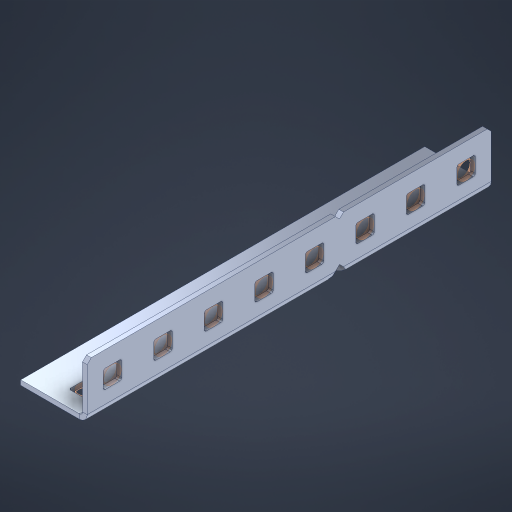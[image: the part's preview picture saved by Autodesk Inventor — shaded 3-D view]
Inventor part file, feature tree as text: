
AUTODESK INVENTOR PART (.ipt)
format: ipt  version: 2023 (Build 270158000, 158)  size: 510,464 bytes
history: native  units: in
note: dims shown in document units (in); Inventor stores cm internally (conversion verified against a paired STEP export)
features: other x21, extrude x15, sheet_metal_op x10, sketch x8, mirror x1, pattern_linear x1, chamfer x1
ambient origin geometry x8: Origin, YZ Plane, XZ Plane, XY Plane, X Axis, Y Axis, Z Axis, Center Point
bodies: Solid1 (feature_tree), Body (feature_tree)
feature tree (57):
  other  "Flange Pattern Plane"
  sheet_metal_op  "Flange Pattern"
  sheet_metal_op  "Body Pattern"
  other  "Arc Length"
  mirror  "Notch Mirror"
  pattern_linear  "Notch Pattern"  Spacing1=0.1875in  [1 undecoded]
  chamfer  "End Chamfer"
  extrude  "Half Cut"  Depth=0.0469in
  sketch  "Sketch1"  dims[d0=2.5in]
  other  "Plate1"
  sketch  "Sketch2"  dims[d1=4.0in]
  other  "Plate2"
  sheet_metal_op  "Bend1"
  sheet_metal_op  "Corner1"
  sketch  "Sketch3"  dims[d2=0.0469in]
  other  "Flange Pattern Sketch"
  sketch  "Sketch7"  dims[d3=0.0469in]
  other  "Srf1"
  other  "Srf2"
  sketch  "Sketch8"  dims[d4=0.0234in]
  sketch  "Sketch9"  dims[d5=0.0938in]
  other  "Srf91"
  sheet_metal_op  "Body Pattern Sketch"
  other  "Srf92"
  sketch  "Sketch13"  dims[d6=0.0469in]
  sketch  "Sketch14"  dims[d7=0.5in d8=90.0deg d9=0.0312in d10=0.1875in d11=0.0469in d12=0.0469in d16=0.182in d17=0.02in d18=0.0469in d19=0.0in d20=0.25in d21=0.25in d46=0.172in d47=1.0in d48=0.0in d49=0.182in d50=0.02in d51=0.25in d52=0.25in d53=0.0469in d54=0.0in d55=0.172in d56=1.0in d57=0.0in d60=3.1496in d62=0.5in d63=0.3937in d65=0.5in d85=0.1227in d86=0.1659in d88=0.04in d89=0.0469in d90=0.0in d91=0.04in d92=0.0491in d95=2.5in d96=0.04in d97=0.25in d98=45.0deg d101=0.0in d102=2.497in d131=0.5in d132=3.1496in d134=0.5in d139=0.5in]
  other  "Srf856"
  other  "Srf1310"
  other  "Srf1311"
  other  "Srf1312"
  other  "Srf1376"
  other  "Srf1377"
  other  "Srf1728"
  other  "Srf1755"
  other  "Srf1878"
  other  "Srf1879"
  other  "Srf1942"
  other  "Srf1943"
  sheet_metal_op  "Flange Stamp"
  sheet_metal_op  "Flange Circle"
  sheet_metal_op  "Body Stamp"
  sheet_metal_op  "Body Circle"
  sheet_metal_op  "Notch"
  extrude  "ExtrusionSrf2"  Depth=0.0469in
  extrude  "ExtrusionSrf92"  Depth=0.5in
  extrude  "ExtrusionSrf856"  Depth=0.02in
  extrude  "ExtrusionSrf1310"  Depth=0.0469in
  extrude  "ExtrusionSrf1311"  TaperAngle=0.0deg  [1 undecoded]
  extrude  "ExtrusionSrf1312"  Depth=0.5in
  extrude  "ExtrusionSrf1376"  Depth=0.5in
  extrude  "ExtrusionSrf1377"  Depth=0.5in
  extrude  "ExtrusionSrf1728"  Depth=0.5in TaperAngle=0.0deg
  extrude  "ExtrusionSrf1755"  Depth=0.5in
  extrude  "ExtrusionSrf1878"  Depth=0.02in
  extrude  "ExtrusionSrf1879"  Depth=0.5in
  extrude  "ExtrusionSrf1942"  Depth=0.5in
  extrude  "ExtrusionSrf1943"  Depth=0.0469in
note: 2 required parameter values undecoded (feature->parameter linkage not recoverable at this tier; creation-order binding heuristic only, values carry confidence <= 0.55)
